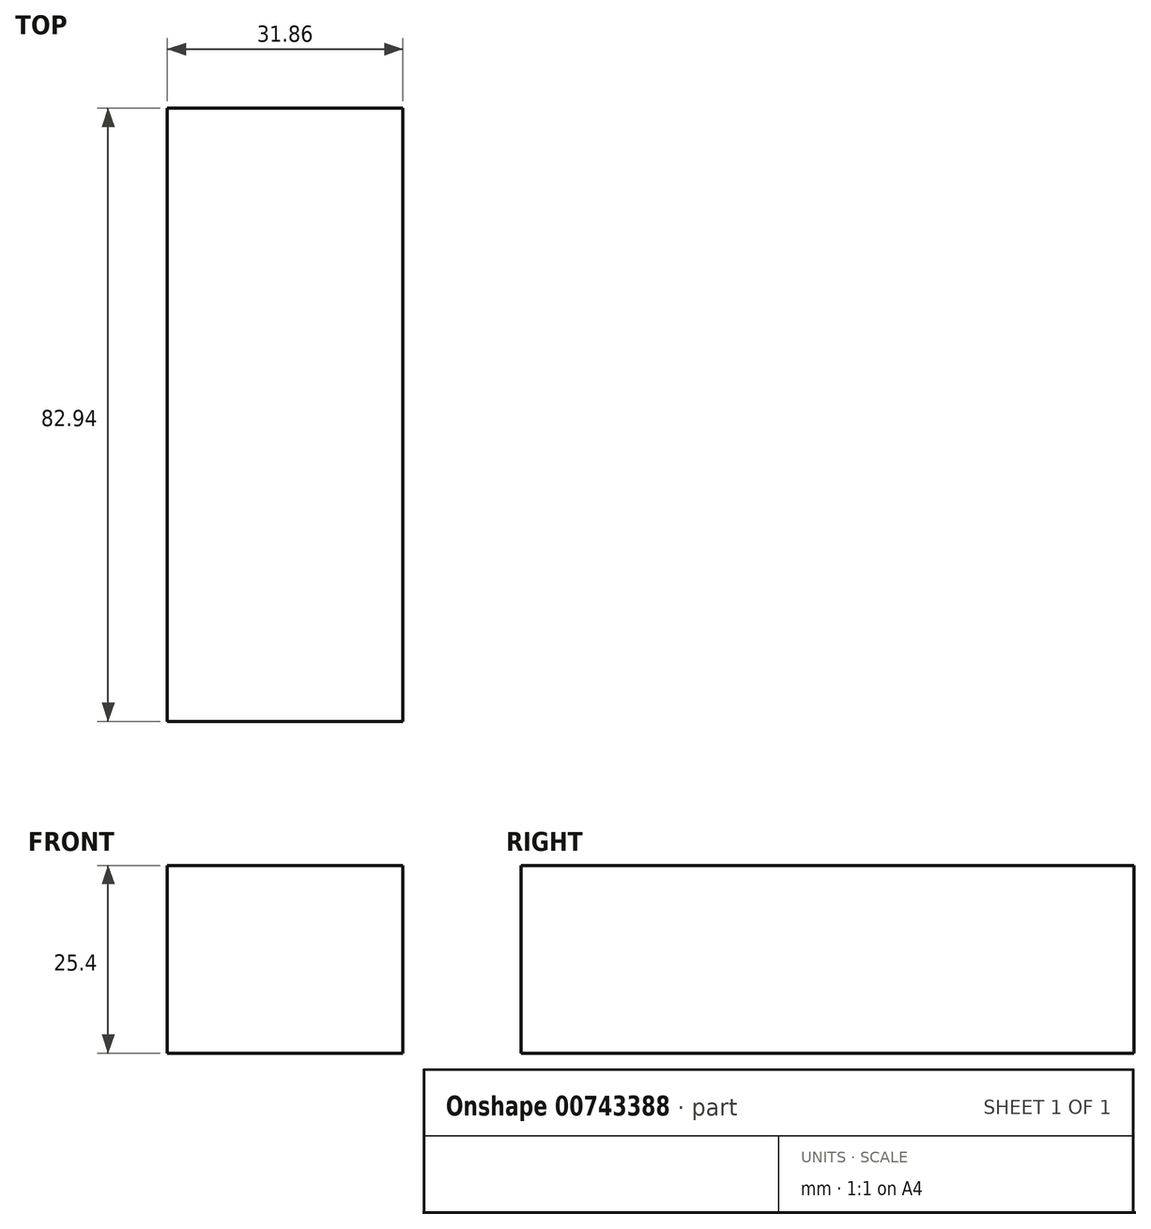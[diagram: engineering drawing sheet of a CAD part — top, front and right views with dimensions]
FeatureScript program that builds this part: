
annotation { "Feature Type Name" : "Feature", "Feature Type Description" : "" }
export const myFeature = defineFeature(function(context is Context, id is Id, definition is map)
    precondition{}
    {
        {
            var Q0;
            Q0=qCreatedBy(makeId("Top.planeOp"),FACE);
            var sketch = newSketch(context, id + "F0", { "sketchPlane" : qUnion([Q0])});
            skLineSegment(sketch, "E0.bottom", {"start": v(-57.2, 0) * mm, "end": v(-25.33, 0) * mm});
            skLineSegment(sketch, "E0.top", {"start": v(-57.2, 82.94) * mm, "end": v(-25.33, 82.94) * mm});
            skLineSegment(sketch, "E0.left", {"start": v(-57.2, 0) * mm, "end": v(-57.2, 82.94) * mm});
            skLineSegment(sketch, "E0.right", {"start": v(-25.33, 0) * mm, "end": v(-25.33, 82.94) * mm});
            skSolve(sketch);
        }
        {
            var Q0;
            Q0 = qSketchRegion(id + "F0", true);
            extrude(context, id + "F1", {"entities" : qUnion([Q0]), "depth" : 25.4 * mm, "offsetDistance" : 25.4 * mm});
        }
    });
